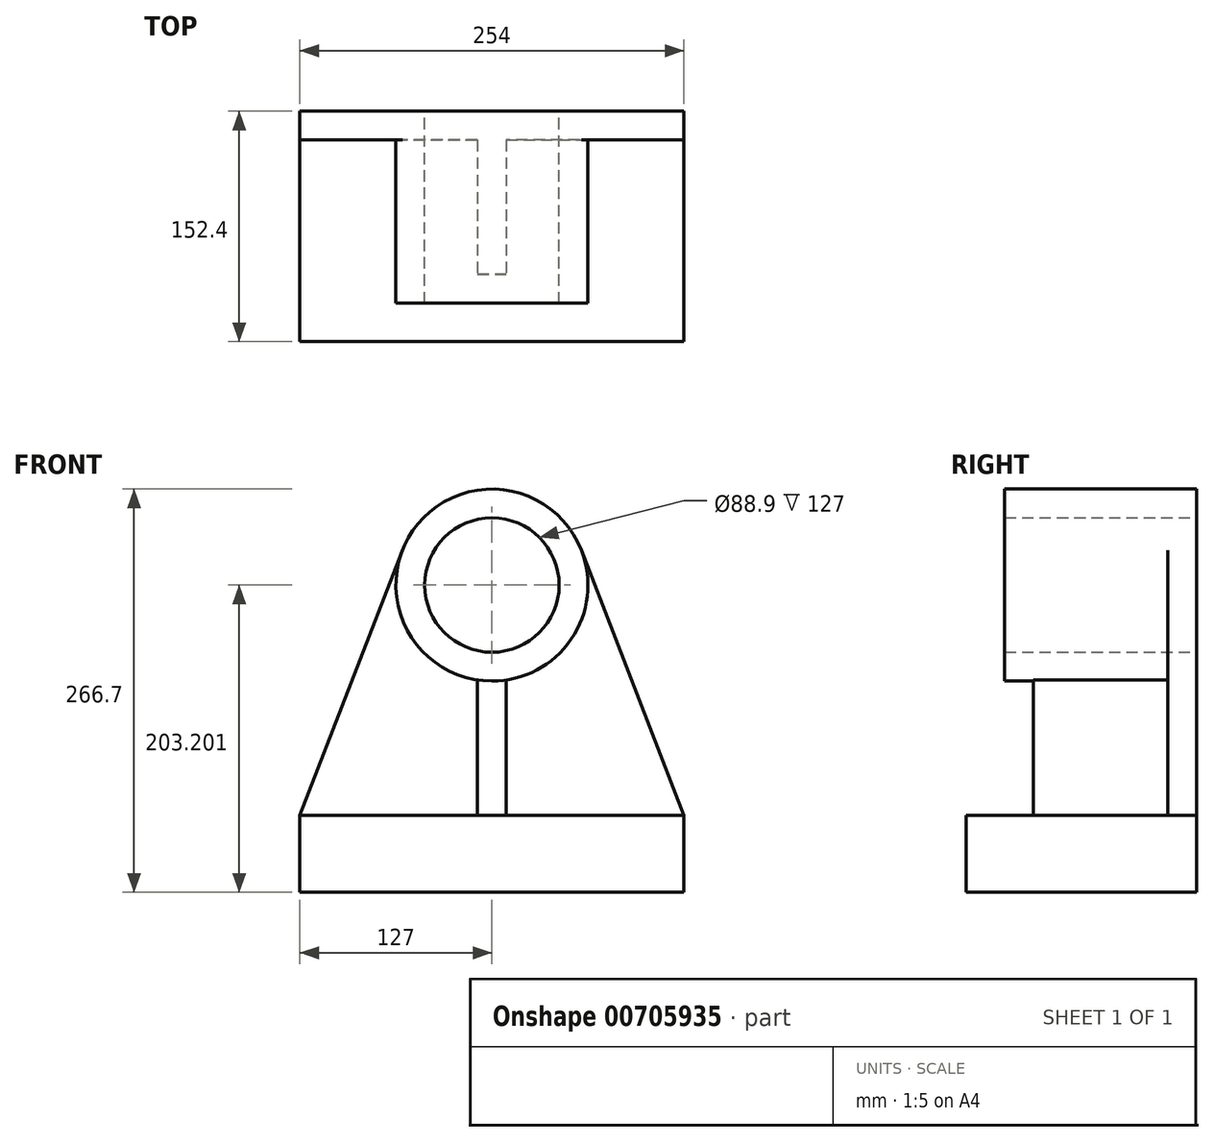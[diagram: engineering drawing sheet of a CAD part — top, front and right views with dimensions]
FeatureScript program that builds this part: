
annotation { "Feature Type Name" : "Feature", "Feature Type Description" : "" }
export const myFeature = defineFeature(function(context is Context, id is Id, definition is map)
    precondition{}
    {
        {
            var Q0;
            Q0=qCreatedBy(makeId("Front.planeOp"),FACE);
            var sketch = newSketch(context, id + "F0", { "sketchPlane" : qUnion([Q0])});
            skLineSegment(sketch, "E0", {"start": v(-127, -155.23) * mm, "end": v(127, -155.23) * mm});
            skLineSegment(sketch, "E1", {"start": v(127, -155.23) * mm, "end": v(127, -104.43) * mm});
            skLineSegment(sketch, "E2", {"start": v(127, -104.43) * mm, "end": v(-127, -104.43) * mm});
            skLineSegment(sketch, "E3", {"start": v(-127, -104.43) * mm, "end": v(-127, -155.23) * mm});
            skLineSegment(sketch, "E4", {"start": v(-127, -104.43) * mm, "end": v(-59.23, 70.87) * mm});
            skLineSegment(sketch, "E5", {"start": v(59.23, 70.87) * mm, "end": v(127, -104.43) * mm});
            skCircle(sketch, "E6", {"center": v(0, 47.97) * mm, "radius": 63.5 * mm});
            skCircle(sketch, "E7", {"center": v(0, 47.97) * mm, "radius": 44.45 * mm});
            skSolve(sketch);
        }
        {
            var Q0;
            Q0=makeQuery(id+"F0.imprint","IMPRINT",FACE,{"disambiguationData":[TD([[makeQuery(id+"F0.imprint","IMPRINT",EDGE,{"derivedFrom":sQuery(id+"F0.wireOp",EDGE,"E0")}),1.0]])]});
            extrude(context, id + "F1", {"entities" : qUnion([Q0]), "depth" : 152.4 * mm, "offsetDistance" : 25.4 * mm});
        }
        {
            var Q0;
            Q0=makeQuery(id+"F0.imprint","IMPRINT",FACE,{"disambiguationData":[TD([[makeQuery(id+"F0.imprint","IMPRINT",EDGE,{"derivedFrom":sQuery(id+"F0.wireOp",EDGE,"E0")}),1.0]])]});
            var Q1;
            Q1=makeQuery(id+"F0.imprint","IMPRINT",FACE,{"disambiguationData":[TD([[makeQuery(id+"F0.imprint","IMPRINT",EDGE,{"derivedFrom":sQuery(id+"F0.wireOp",EDGE,"E2")}),-1.0]])]});
            extrude(context, id + "F2", {"entities" : qUnion([Q0, Q1]), "operationType" : NewBodyOperationType.ADD, "depth" : 19.05 * mm, "offsetDistance" : 25.4 * mm});
        }
        {
            var Q0;
            Q0=makeQuery(id+"F0.imprint","IMPRINT",FACE,{"disambiguationData":[TD([[makeQuery(id+"F0.imprint","IMPRINT",EDGE,{"derivedFrom":sQuery(id+"F0.wireOp",EDGE,"E7")}),-1.0]])]});
            extrude(context, id + "F3", {"entities" : qUnion([Q0]), "operationType" : NewBodyOperationType.ADD, "depth" : 127 * mm, "offsetDistance" : 25.4 * mm});
        }
        {
            var Q0;
            Q0=qCreatedBy(makeId("Right.planeOp"),FACE);
            var sketch = newSketch(context, id + "F4", { "sketchPlane" : qUnion([Q0])});
            skLineSegment(sketch, "E8", {"start": v(-107.95, -11.26) * mm, "end": v(-107.95, -113.02) * mm});
            skLineSegment(sketch, "E9", {"start": v(-107.95, -113.02) * mm, "end": v(-13.85, -113.02) * mm});
            skLineSegment(sketch, "E10", {"start": v(-13.85, -113.02) * mm, "end": v(-13.85, -10.1) * mm});
            skLineSegment(sketch, "E11", {"start": v(-13.85, -10.1) * mm, "end": v(-107.95, -11.26) * mm});
            skSolve(sketch);
        }
        {
            var Q0;
            Q0 = qSketchRegion(id + "F4", true);
            extrude(context, id + "F5", {"entities" : qUnion([Q0]), "operationType" : NewBodyOperationType.ADD, "endBound" : BoundingType.SYMMETRIC, "depth" : 19.05 * mm, "offsetDistance" : 25.4 * mm});
        }
    });
